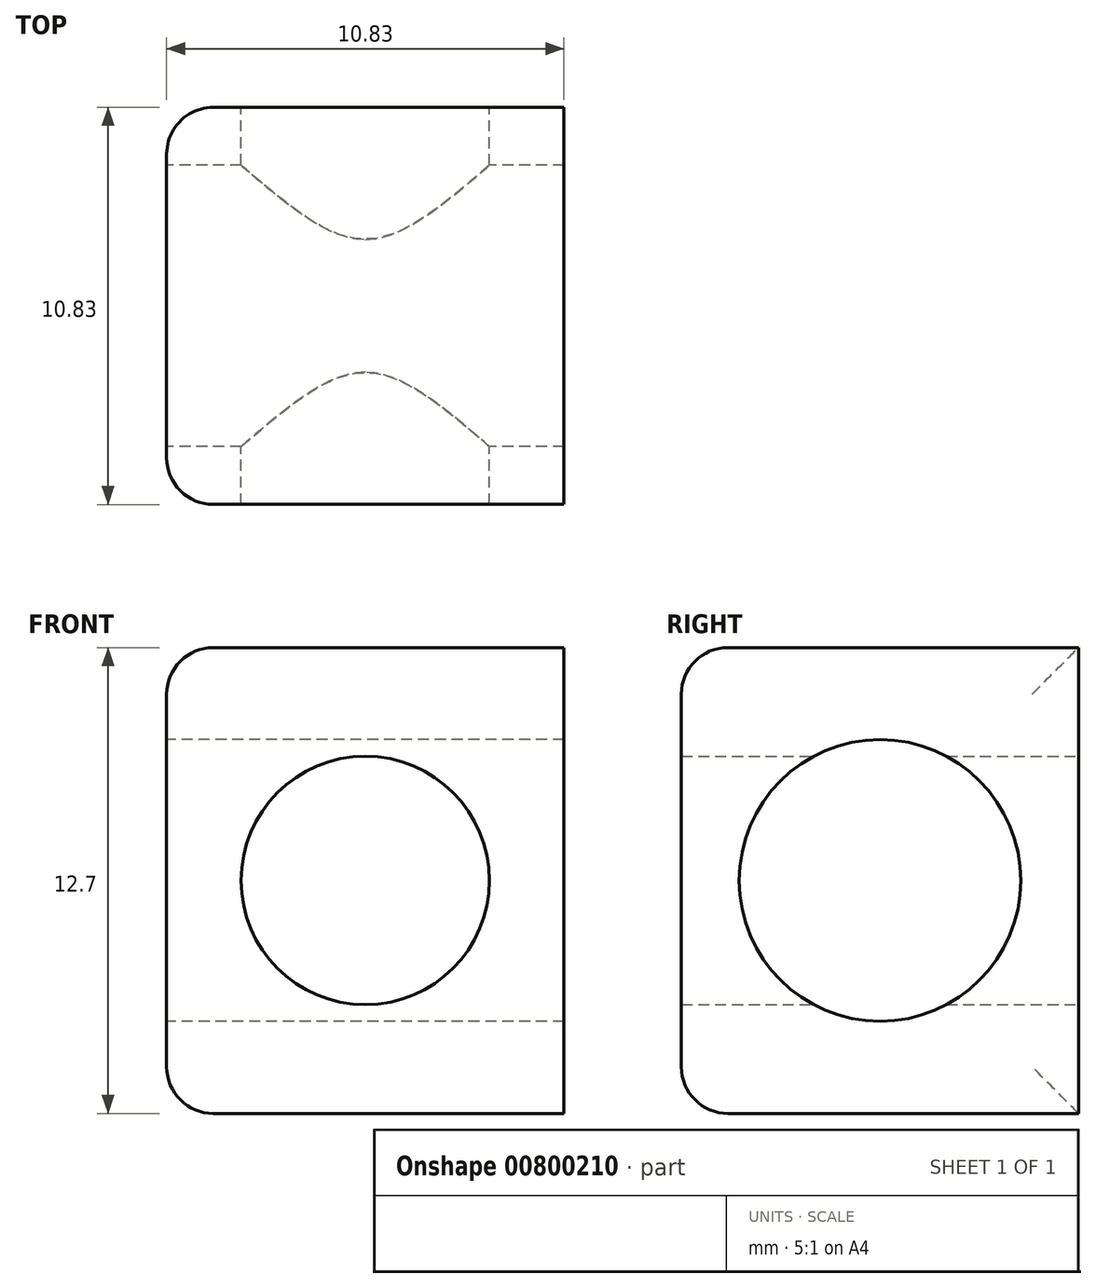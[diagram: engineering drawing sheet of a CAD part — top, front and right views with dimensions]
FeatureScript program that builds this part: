
annotation { "Feature Type Name" : "Feature", "Feature Type Description" : "" }
export const myFeature = defineFeature(function(context is Context, id is Id, definition is map)
    precondition{}
    {
        {
            var Q0;
            Q0=qCreatedBy(makeId("Top.planeOp"),FACE);
            var sketch = newSketch(context, id + "F0", { "sketchPlane" : qUnion([Q0])});
            skLineSegment(sketch, "E0.bottom", {"start": v(-34.14, 45.57) * mm, "end": v(-23.31, 45.57) * mm});
            skLineSegment(sketch, "E0.top", {"start": v(-34.14, 34.74) * mm, "end": v(-23.31, 34.74) * mm});
            skLineSegment(sketch, "E0.left", {"start": v(-34.14, 45.57) * mm, "end": v(-34.14, 34.74) * mm});
            skLineSegment(sketch, "E0.right", {"start": v(-23.31, 45.57) * mm, "end": v(-23.31, 34.74) * mm});
            skSolve(sketch);
        }
        {
            var Q0;
            Q0 = qSketchRegion(id + "F0", true);
            extrude(context, id + "F1", {"entities" : qUnion([Q0]), "depth" : 12.7 * mm, "offsetDistance" : 25.4 * mm});
        }
        {
            var Q0;
            Q0=makeQuery(id+"F1.opExtrude","SWEPT_FACE",FACE,{"disambiguationData":[OSD([sQuery(id+"F0.wireOp",EDGE,"E0.left")])]});
            var sketch = newSketch(context, id + "F2", { "sketchPlane" : qUnion([Q0])});
            skCircle(sketch, "E1", {"center": v(-40.16, 6.35) * mm, "radius": 3.84 * mm});
            skSolve(sketch);
        }
        {
            var Q0;
            Q0 = qSketchRegion(id + "F2", true);
            extrude(context, id + "F3", {"entities" : qUnion([Q0]), "operationType" : NewBodyOperationType.REMOVE, "oppositeDirection" : true, "depth" : 25.4 * mm, "offsetDistance" : 25.4 * mm});
        }
        {
            var Q0;
            Q0=makeQuery(id+"F1.opExtrude","SWEPT_FACE",FACE,{"disambiguationData":[OSD([sQuery(id+"F0.wireOp",EDGE,"E0.bottom")])]});
            var sketch = newSketch(context, id + "F4", { "sketchPlane" : qUnion([Q0])});
            skCircle(sketch, "E2", {"center": v(28.73, 6.35) * mm, "radius": 3.39 * mm});
            skSolve(sketch);
        }
        {
            var Q0;
            Q0=makeQuery(id+"F4.imprint","IMPRINT",FACE,{"disambiguationData":[TD([[makeQuery(id+"F4.imprint","IMPRINT",EDGE,{"derivedFrom":sQuery(id+"F4.wireOp",EDGE,"E2")}),1.0]])]});
            extrude(context, id + "F5", {"entities" : qUnion([Q0]), "operationType" : NewBodyOperationType.REMOVE, "oppositeDirection" : true, "depth" : 25.4 * mm, "offsetDistance" : 25.4 * mm});
        }
        {
            var Q0;
            Q0=makeQuery(id+"F1.opExtrude","CAP_EDGE",EDGE,{"disambiguationData":[OSD([sQuery(id+"F0.wireOp",EDGE,"E0.left")])],"isStart":false});
            var Q1;
            Q1=makeQuery(id+"F1.opExtrude","SWEPT_EDGE",EDGE,{"disambiguationData":[OSD([sQuery(id+"F0.wireOp",EDGE,"E0.bottom"),sQuery(id+"F0.wireOp",EDGE,"E0.left")])]});
            var Q2;
            Q2=makeQuery(id+"F1.opExtrude","CAP_EDGE",EDGE,{"disambiguationData":[OSD([sQuery(id+"F0.wireOp",EDGE,"E0.left")])],"isStart":true});
            var Q3;
            Q3=makeQuery(id+"F1.opExtrude","SWEPT_EDGE",EDGE,{"disambiguationData":[OSD([sQuery(id+"F0.wireOp",EDGE,"E0.top"),sQuery(id+"F0.wireOp",EDGE,"E0.left")])]});
            var Q4;
            Q4=makeQuery(id+"F1.opExtrude","CAP_EDGE",EDGE,{"disambiguationData":[OSD([sQuery(id+"F0.wireOp",EDGE,"E0.top")])],"isStart":false});
            var Q5;
            Q5=makeQuery(id+"F1.opExtrude","CAP_EDGE",EDGE,{"disambiguationData":[OSD([sQuery(id+"F0.wireOp",EDGE,"E0.top")])],"isStart":true});
            fillet(context, id + "F6", {"entities" : qUnion([Q0, Q1, Q2, Q3, Q4, Q5]), "radius" : 1.27 * mm, "tangentPropagation" : true, "allowEdgeOverflow" : false});
        }
    });
